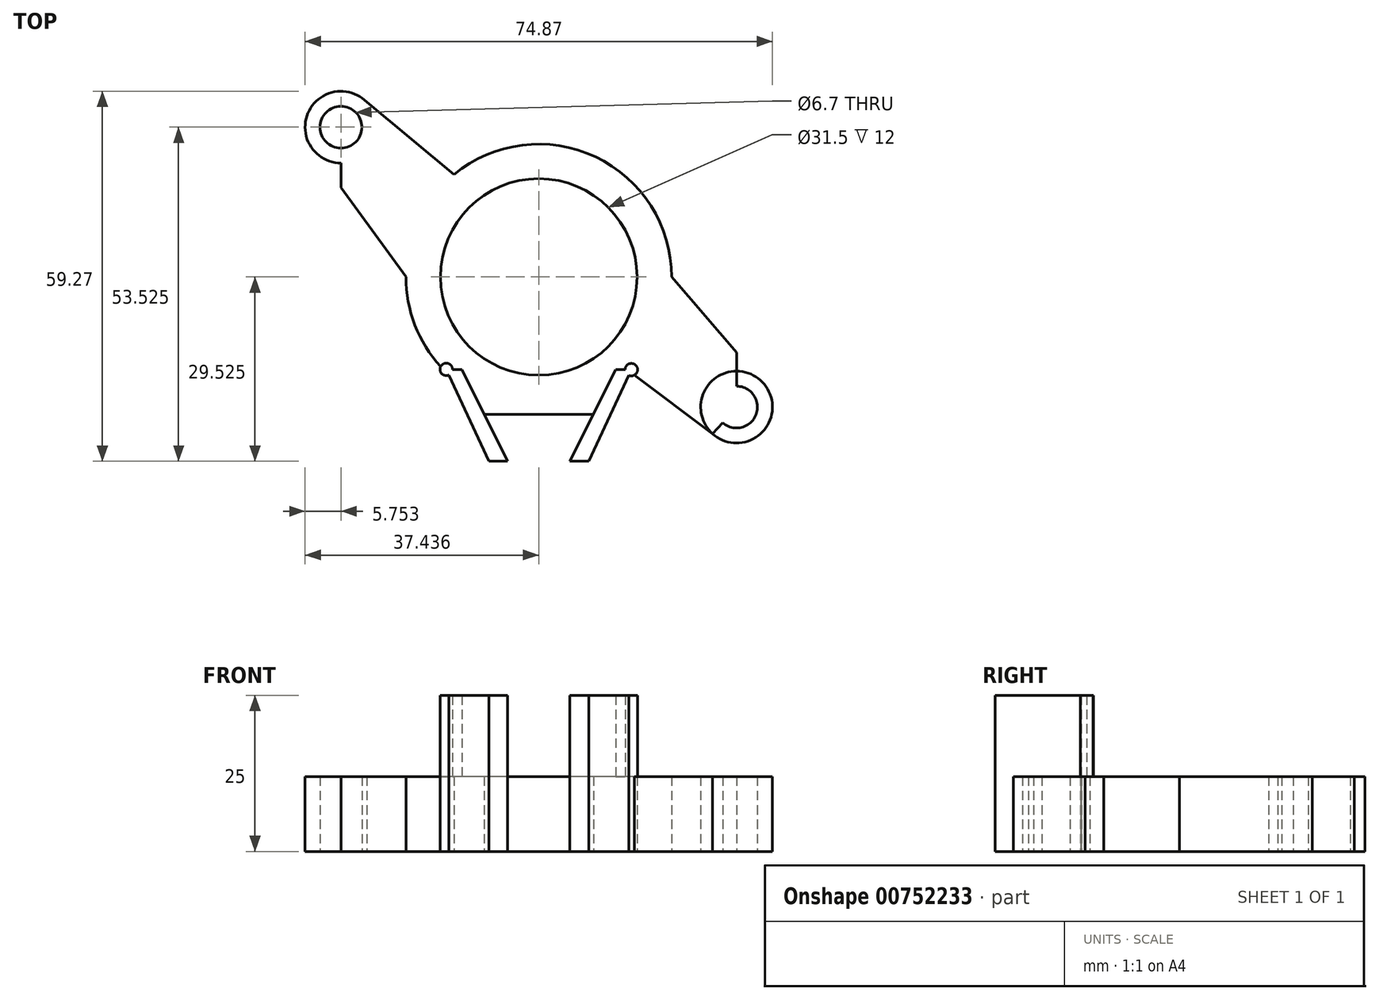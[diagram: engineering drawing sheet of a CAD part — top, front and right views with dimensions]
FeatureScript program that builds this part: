
annotation { "Feature Type Name" : "Feature", "Feature Type Description" : "" }
export const myFeature = defineFeature(function(context is Context, id is Id, definition is map)
    precondition{}
    {
        {
            var Q0;
            Q0=qCreatedBy(makeId("Top.planeOp"),FACE);
            var sketch = newSketch(context, id + "F0", { "sketchPlane" : qUnion([Q0])});
            skLineSegment(sketch, "E0.bottom", {"start": v(-52.47, 39.18) * mm, "end": v(4.2, 39.18) * mm});
            skLineSegment(sketch, "E0.left", {"start": v(-55.82, 35.83) * mm, "end": v(-55.82, -5.47) * mm});
            skLineSegment(sketch, "E0.right", {"start": v(7.55, 35.83) * mm, "end": v(7.55, -2.3) * mm});
            skCircle(sketch, "E1", {"center": v(7.55, 39.18) * mm, "radius": 3.35 * mm});
            skCircle(sketch, "E2", {"center": v(-55.82, 39.18) * mm, "radius": 3.35 * mm});
            skCircle(sketch, "E3", {"center": v(-55.82, -8.82) * mm, "radius": 3.35 * mm});
            skCircle(sketch, "E4", {"center": v(7.55, -5.66) * mm, "radius": 3.35 * mm});
            skCircle(sketch, "E5", {"center": v(-55.82, 39.18) * mm, "radius": 5.75 * mm});
            skCircle(sketch, "E6", {"center": v(7.55, 39.18) * mm, "radius": 5.75 * mm});
            skCircle(sketch, "E7", {"center": v(7.55, -5.66) * mm, "radius": 5.75 * mm});
            skCircle(sketch, "E8", {"center": v(-55.82, -8.82) * mm, "radius": 5.75 * mm});
            skPoint(sketch, "E9.first.point", {"position": v(-24.13, 39.18) * mm});
            skPoint(sketch, "E9.second.point", {"position": v(-55.82, 15.18) * mm});
            skPoint(sketch, "E10.middle", {"position": v(-24.13, 15.18) * mm});
            skCircle(sketch, "E11", {"center": v(-24.13, 15.18) * mm, "radius": 15.75 * mm});
            skLineSegment(sketch, "E12", {"start": v(-24.13, -6.82) * mm, "end": v(-24.13, -7.85) * mm});
            skLineSegment(sketch, "E13", {"start": v(-36.46, 0.34) * mm, "end": v(-29.13, -14.34) * mm});
            skLineSegment(sketch, "E14", {"start": v(-19.13, -14.34) * mm, "end": v(-11.8, 0.34) * mm});
            skLineSegment(sketch, "E15", {"start": v(-29.13, -14.34) * mm, "end": v(-32.13, -14.34) * mm});
            skLineSegment(sketch, "E16", {"start": v(-32.13, -14.34) * mm, "end": v(-38.96, 0.4) * mm});
            skLineSegment(sketch, "E17", {"start": v(-38.96, 0.4) * mm, "end": v(-36.46, 0.34) * mm});
            skLineSegment(sketch, "E18", {"start": v(-19.13, -14.34) * mm, "end": v(-16.13, -14.34) * mm});
            skLineSegment(sketch, "E19", {"start": v(-16.13, -14.34) * mm, "end": v(-9.3, 0.34) * mm});
            skLineSegment(sketch, "E20", {"start": v(-9.3, 0.34) * mm, "end": v(-11.8, 0.34) * mm});
            skLineSegment(sketch, "E21.trimOffspring", {"start": v(-55.82, -8.82) * mm, "end": v(-55.82, -8.82) * mm});
            skLineSegment(sketch, "E22.trimOffspring", {"start": v(7.55, 39.18) * mm, "end": v(7.55, 39.18) * mm});
            skPoint(sketch, "E23.orphan", {"position": v(-24.13, -14.34) * mm});
            skLineSegment(sketch, "E24", {"start": v(-24.13, 15.18) * mm, "end": v(-42.63, 15.18) * mm});
            skLineSegment(sketch, "E25", {"start": v(-36.46, 0.34) * mm, "end": v(-42.63, 15.18) * mm});
            skLineSegment(sketch, "E26", {"start": v(-24.13, 15.18) * mm, "end": v(-5.63, 15.18) * mm});
            skLineSegment(sketch, "E27", {"start": v(-11.8, 0.34) * mm, "end": v(-5.63, 15.18) * mm});
            skLineSegment(sketch, "E28", {"start": v(-29.13, -14.34) * mm, "end": v(-19.13, -14.34) * mm});
            skLineSegment(sketch, "E29", {"start": v(-42.63, 15.18) * mm, "end": v(-55.82, 15.18) * mm});
            skLineSegment(sketch, "E30", {"start": v(-5.63, 15.18) * mm, "end": v(7.55, 15.18) * mm});
            skLineSegment(sketch, "E31", {"start": v(-24.13, 15.18) * mm, "end": v(-24.13, -14.34) * mm});
            skLineSegment(sketch, "E32", {"start": v(-24.13, 15.18) * mm, "end": v(-24.13, 39.18) * mm});
            skLineSegment(sketch, "E33", {"start": v(-24.13, -6.82) * mm, "end": v(1.92, -6.82) * mm});
            skLineSegment(sketch, "E34", {"start": v(-24.13, -6.82) * mm, "end": v(-50.43, -6.82) * mm});
            skLineSegment(sketch, "E35", {"start": v(7.55, -5.66) * mm, "end": v(11.38, -1.37) * mm});
            skLineSegment(sketch, "E36", {"start": v(11.38, -1.37) * mm, "end": v(7.55, -5.66) * mm});
            skLineSegment(sketch, "E37", {"start": v(7.55, -5.66) * mm, "end": v(3.72, -9.95) * mm});
            skLineSegment(sketch, "E38", {"start": v(-55.82, 39.18) * mm, "end": v(-59.94, 35.18) * mm});
            skLineSegment(sketch, "E39", {"start": v(-55.82, 39.18) * mm, "end": v(-51.7, 43.2) * mm});
            skArc(sketch, "E40", {"start": v(-2.85, 15.18) * mm, "mid": v(-32.67, 34.68) * mm, "end": v(-38.57, -0.46) * mm});
            skLineSegment(sketch, "E41", {"start": v(11.38, -1.37) * mm, "end": v(-2.85, 15.18) * mm});
            skLineSegment(sketch, "E42", {"start": v(-51.7, 43.2) * mm, "end": v(-37.7, 31.59) * mm});
            skLineSegment(sketch, "E43", {"start": v(-59.94, 35.18) * mm, "end": v(-45.42, 15.18) * mm});
            skLineSegment(sketch, "E44", {"start": v(3.72, -9.95) * mm, "end": v(-9.47, 0) * mm});
            skLineSegment(sketch, "E45", {"start": v(-36.46, 0.34) * mm, "end": v(-24.13, 0.34) * mm});
            skLineSegment(sketch, "E46", {"start": v(-24.13, 0.34) * mm, "end": v(-11.8, 0.34) * mm});
            skLineSegment(sketch, "E47", {"start": v(-38.96, 0.4) * mm, "end": v(-39.44, 0.4) * mm});
            skCircle(sketch, "E48", {"center": v(-9.3, 0.34) * mm, "radius": 1 * mm});
            skCircle(sketch, "E49", {"center": v(-38.96, 0.4) * mm, "radius": 1 * mm});
            skSolve(sketch);
        }
        {
            var Q0;
            {var subQ0=sQuery(id+"F0.wireOp",EDGE,"E39");var subQ1=sQuery(id+"F0.wireOp",EDGE,"E2");var subQ2=makeQuery(id+"F0.imprint","INTERSECT",VERTEX,{"derivedFrom":[subQ1,subQ0]});Q0=makeQuery(id+"F0.imprint","IMPRINT",FACE,{"disambiguationData":[TD([[makeQuery(id+"F0.imprint","IMPRINT",EDGE,{"disambiguationData":[TD([[subQ2,-1.0]])],"derivedFrom":subQ1}),-1.0]])]});}
            var Q1;
            {var subQ0=sQuery(id+"F0.wireOp",EDGE,"E0.bottom");var subQ1=sQuery(id+"F0.wireOp",EDGE,"E2");var subQ2=makeQuery(id+"F0.imprint","INTERSECT",VERTEX,{"derivedFrom":[subQ1,subQ0]});Q1=makeQuery(id+"F0.imprint","IMPRINT",FACE,{"disambiguationData":[TD([[makeQuery(id+"F0.imprint","IMPRINT",EDGE,{"disambiguationData":[TD([[subQ2,-1.0]])],"derivedFrom":subQ1}),-1.0]])]});}
            var Q2;
            {var subQ0=sQuery(id+"F0.wireOp",EDGE,"E42");var subQ3=sQuery(id+"F0.wireOp",EDGE,"E0.bottom");var subQ5=makeQuery(id+"F0.imprint","INTERSECT",VERTEX,{"derivedFrom":[subQ3,subQ0]});Q2=makeQuery(id+"F0.imprint","IMPRINT",FACE,{"disambiguationData":[TD([[makeQuery(id+"F0.imprint","IMPRINT",EDGE,{"disambiguationData":[TD([[subQ5,1.0]])],"derivedFrom":subQ3}),1.0]])]});}
            var Q3;
            {var subQ0=sQuery(id+"F0.wireOp",EDGE,"E0.left");var subQ1=sQuery(id+"F0.wireOp",EDGE,"E2");var subQ2=makeQuery(id+"F0.imprint","INTERSECT",VERTEX,{"derivedFrom":[subQ1,subQ0]});Q3=makeQuery(id+"F0.imprint","IMPRINT",FACE,{"disambiguationData":[TD([[makeQuery(id+"F0.imprint","IMPRINT",EDGE,{"disambiguationData":[TD([[subQ2,1.0]])],"derivedFrom":subQ1}),-1.0]])]});}
            var Q4;
            {var subQ0=sQuery(id+"F0.wireOp",EDGE,"E0.bottom");var subQ1=sQuery(id+"F0.wireOp",EDGE,"E2");var subQ2=makeQuery(id+"F0.imprint","INTERSECT",VERTEX,{"derivedFrom":[subQ1,subQ0]});Q4=makeQuery(id+"F0.imprint","IMPRINT",FACE,{"disambiguationData":[TD([[makeQuery(id+"F0.imprint","IMPRINT",EDGE,{"disambiguationData":[TD([[subQ2,1.0]])],"derivedFrom":subQ1}),-1.0]])]});}
            var Q5;
            {var subQ0=sQuery(id+"F0.wireOp",EDGE,"E43");var subQ3=sQuery(id+"F0.wireOp",EDGE,"E0.left");var subQ5=makeQuery(id+"F0.imprint","INTERSECT",VERTEX,{"derivedFrom":[subQ3,subQ0]});Q5=makeQuery(id+"F0.imprint","IMPRINT",FACE,{"disambiguationData":[TD([[makeQuery(id+"F0.imprint","IMPRINT",EDGE,{"disambiguationData":[TD([[subQ5,1.0]])],"derivedFrom":subQ3}),-1.0]])]});}
            var Q6;
            {var subQ7=sQuery(id+"F0.wireOp",EDGE,"E5");var subQ9=sQuery(id+"F0.wireOp",EDGE,"E0.bottom");var subQ11=makeQuery(id+"F0.imprint","INTERSECT",VERTEX,{"derivedFrom":[subQ7,subQ9]});Q6=makeQuery(id+"F0.imprint","IMPRINT",FACE,{"disambiguationData":[TD([[makeQuery(id+"F0.imprint","IMPRINT",EDGE,{"disambiguationData":[TD([[subQ11,1.0]])],"derivedFrom":subQ7}),-1.0]])]});}
            var Q7;
            {var subQ0=sQuery(id+"F0.wireOp",EDGE,"E32");var subQ1=sQuery(id+"F0.wireOp",EDGE,"E11");var subQ2=makeQuery(id+"F0.imprint","INTERSECT",VERTEX,{"derivedFrom":[subQ1,subQ0]});Q7=makeQuery(id+"F0.imprint","IMPRINT",FACE,{"disambiguationData":[TD([[makeQuery(id+"F0.imprint","IMPRINT",EDGE,{"disambiguationData":[TD([[subQ2,-1.0]])],"derivedFrom":subQ1}),-1.0]])]});}
            var Q8;
            {var subQ0=sQuery(id+"F0.wireOp",EDGE,"E32");var subQ1=sQuery(id+"F0.wireOp",EDGE,"E11");var subQ2=makeQuery(id+"F0.imprint","INTERSECT",VERTEX,{"derivedFrom":[subQ1,subQ0]});Q8=makeQuery(id+"F0.imprint","IMPRINT",FACE,{"disambiguationData":[TD([[makeQuery(id+"F0.imprint","IMPRINT",EDGE,{"disambiguationData":[TD([[subQ2,1.0]])],"derivedFrom":subQ1}),-1.0]])]});}
            var Q9;
            {var subQ0=sQuery(id+"F0.wireOp",EDGE,"E27");Q9=makeQuery(id+"F0.imprint","IMPRINT",FACE,{"disambiguationData":[TD([[makeQuery(id+"F0.imprint","IMPRINT",EDGE,{"derivedFrom":subQ0}),-1.0]])]});}
            var Q10;
            {var subQ5=sQuery(id+"F0.wireOp",EDGE,"E27");Q10=makeQuery(id+"F0.imprint","IMPRINT",FACE,{"disambiguationData":[TD([[makeQuery(id+"F0.imprint","IMPRINT",EDGE,{"derivedFrom":subQ5}),1.0]])]});}
            var Q11;
            {var subQ0=sQuery(id+"F0.wireOp",EDGE,"E0.right");var subQ1=sQuery(id+"F0.wireOp",EDGE,"E4");var subQ2=makeQuery(id+"F0.imprint","INTERSECT",VERTEX,{"derivedFrom":[subQ1,subQ0]});Q11=makeQuery(id+"F0.imprint","IMPRINT",FACE,{"disambiguationData":[TD([[makeQuery(id+"F0.imprint","IMPRINT",EDGE,{"disambiguationData":[TD([[subQ2,-1.0]])],"derivedFrom":subQ1}),-1.0]])]});}
            var Q12;
            {var subQ0=sQuery(id+"F0.wireOp",EDGE,"E0.right");var subQ1=sQuery(id+"F0.wireOp",EDGE,"E4");var subQ2=makeQuery(id+"F0.imprint","INTERSECT",VERTEX,{"derivedFrom":[subQ1,subQ0]});Q12=makeQuery(id+"F0.imprint","IMPRINT",FACE,{"disambiguationData":[TD([[makeQuery(id+"F0.imprint","IMPRINT",EDGE,{"disambiguationData":[TD([[subQ2,1.0]])],"derivedFrom":subQ1}),-1.0]])]});}
            var Q13;
            {var subQ0=sQuery(id+"F0.wireOp",EDGE,"E36");var subQ1=sQuery(id+"F0.wireOp",EDGE,"E4");var subQ2=makeQuery(id+"F0.imprint","INTERSECT",VERTEX,{"derivedFrom":[subQ1,subQ0]});Q13=makeQuery(id+"F0.imprint","IMPRINT",FACE,{"disambiguationData":[TD([[makeQuery(id+"F0.imprint","IMPRINT",EDGE,{"disambiguationData":[TD([[subQ2,1.0]])],"derivedFrom":subQ1}),-1.0]])]});}
            var Q14;
            {var subQ0=sQuery(id+"F0.wireOp",EDGE,"E33");var subQ1=sQuery(id+"F0.wireOp",EDGE,"E19");var subQ2=makeQuery(id+"F0.imprint","INTERSECT",VERTEX,{"derivedFrom":[subQ1,subQ0]});Q14=makeQuery(id+"F0.imprint","IMPRINT",FACE,{"disambiguationData":[TD([[makeQuery(id+"F0.imprint","IMPRINT",EDGE,{"disambiguationData":[TD([[subQ2,-1.0]])],"derivedFrom":subQ1}),1.0]])]});}
            var Q15;
            {var subQ0=sQuery(id+"F0.wireOp",EDGE,"E18");Q15=makeQuery(id+"F0.imprint","IMPRINT",FACE,{"disambiguationData":[TD([[makeQuery(id+"F0.imprint","IMPRINT",EDGE,{"derivedFrom":subQ0}),1.0]])]});}
            var Q16;
            {var subQ0=sQuery(id+"F0.wireOp",EDGE,"E31");var subQ3=makeQuery(id+"F0.imprint","IMPRINT",VERTEX,{"derivedFrom":subQ0});Q16=makeQuery(id+"F0.imprint","IMPRINT",FACE,{"disambiguationData":[TD([[makeQuery(id+"F0.imprint","IMPRINT",EDGE,{"disambiguationData":[TD([[subQ3,-1.0]])],"derivedFrom":subQ0}),1.0]])]});}
            var Q17;
            {var subQ0=sQuery(id+"F0.wireOp",EDGE,"E15");Q17=makeQuery(id+"F0.imprint","IMPRINT",FACE,{"disambiguationData":[TD([[makeQuery(id+"F0.imprint","IMPRINT",EDGE,{"derivedFrom":subQ0}),-1.0]])]});}
            var Q18;
            {var subQ1=sQuery(id+"F0.wireOp",EDGE,"E31");var subQ3=makeQuery(id+"F0.imprint","IMPRINT",VERTEX,{"derivedFrom":subQ1});Q18=makeQuery(id+"F0.imprint","IMPRINT",FACE,{"disambiguationData":[TD([[makeQuery(id+"F0.imprint","IMPRINT",EDGE,{"disambiguationData":[TD([[subQ3,-1.0]])],"derivedFrom":subQ1}),-1.0]])]});}
            var Q19;
            {var subQ0=sQuery(id+"F0.wireOp",EDGE,"E34");var subQ1=sQuery(id+"F0.wireOp",EDGE,"E16");var subQ2=makeQuery(id+"F0.imprint","INTERSECT",VERTEX,{"derivedFrom":[subQ1,subQ0]});Q19=makeQuery(id+"F0.imprint","IMPRINT",FACE,{"disambiguationData":[TD([[makeQuery(id+"F0.imprint","IMPRINT",EDGE,{"disambiguationData":[TD([[subQ2,-1.0]])],"derivedFrom":subQ1}),-1.0]])]});}
            var Q20;
            {var subQ0=sQuery(id+"F0.wireOp",EDGE,"E45");var subQ7=sQuery(id+"F0.wireOp",EDGE,"E11");var subQ9=makeQuery(id+"F0.imprint","INTERSECT",VERTEX,{"derivedFrom":[subQ7,subQ0]});Q20=makeQuery(id+"F0.imprint","IMPRINT",FACE,{"disambiguationData":[TD([[makeQuery(id+"F0.imprint","IMPRINT",EDGE,{"disambiguationData":[TD([[subQ9,-1.0]])],"derivedFrom":subQ7}),-1.0]])]});}
            var Q21;
            {var subQ1=sQuery(id+"F0.wireOp",EDGE,"E31");var subQ3=sQuery(id+"F0.wireOp",EDGE,"E11");var subQ4=makeQuery(id+"F0.imprint","INTERSECT",VERTEX,{"derivedFrom":[subQ3,subQ1]});Q21=makeQuery(id+"F0.imprint","IMPRINT",FACE,{"disambiguationData":[TD([[makeQuery(id+"F0.imprint","IMPRINT",EDGE,{"disambiguationData":[TD([[subQ4,-1.0]])],"derivedFrom":subQ3}),-1.0]])]});}
            var Q22;
            {var subQ5=sQuery(id+"F0.wireOp",EDGE,"E25");Q22=makeQuery(id+"F0.imprint","IMPRINT",FACE,{"disambiguationData":[TD([[makeQuery(id+"F0.imprint","IMPRINT",EDGE,{"derivedFrom":subQ5}),-1.0]])]});}
            var Q23;
            {var subQ7=sQuery(id+"F0.wireOp",EDGE,"E25");Q23=makeQuery(id+"F0.imprint","IMPRINT",FACE,{"disambiguationData":[TD([[makeQuery(id+"F0.imprint","IMPRINT",EDGE,{"derivedFrom":subQ7}),1.0]])]});}
            var Q24;
            {var subQ0=sQuery(id+"F0.wireOp",EDGE,"E16");var subQ1=makeQuery(id+"F0.imprint","INTERSECT",VERTEX,{"derivedFrom":[subQ0,sQuery(id+"F0.wireOp",EDGE,"E40")]});Q24=makeQuery(id+"F0.imprint","IMPRINT",FACE,{"disambiguationData":[TD([[makeQuery(id+"F0.imprint","IMPRINT",EDGE,{"disambiguationData":[TD([[subQ1,1.0]])],"derivedFrom":subQ0}),-1.0]])]});}
            var Q25;
            {var subQ0=sQuery(id+"F0.wireOp",EDGE,"E47");Q25=makeQuery(id+"F0.imprint","IMPRINT",FACE,{"disambiguationData":[TD([[makeQuery(id+"F0.imprint","IMPRINT",EDGE,{"derivedFrom":subQ0}),-1.0]])]});}
            var Q26;
            {var subQ0=sQuery(id+"F0.wireOp",EDGE,"E40");var subQ1=sQuery(id+"F0.wireOp",EDGE,"E16");var subQ2=makeQuery(id+"F0.imprint","INTERSECT",VERTEX,{"derivedFrom":[subQ1,subQ0]});Q26=makeQuery(id+"F0.imprint","IMPRINT",FACE,{"disambiguationData":[TD([[makeQuery(id+"F0.imprint","IMPRINT",EDGE,{"disambiguationData":[TD([[subQ2,1.0]])],"derivedFrom":subQ1}),1.0]])]});}
            var Q27;
            {var subQ0=sQuery(id+"F0.wireOp",EDGE,"E33");var subQ1=sQuery(id+"F0.wireOp",EDGE,"E7");var subQ2=makeQuery(id+"F0.imprint","INTERSECT",VERTEX,{"derivedFrom":[subQ1,subQ0]});Q27=makeQuery(id+"F0.imprint","IMPRINT",FACE,{"disambiguationData":[TD([[makeQuery(id+"F0.imprint","IMPRINT",EDGE,{"disambiguationData":[TD([[subQ2,1.0]])],"derivedFrom":subQ0}),-1.0]])]});}
            var Q28;
            {var subQ0=sQuery(id+"F0.wireOp",EDGE,"E41");var subQ3=sQuery(id+"F0.wireOp",EDGE,"E0.right");var subQ5=makeQuery(id+"F0.imprint","INTERSECT",VERTEX,{"derivedFrom":[subQ3,subQ0]});Q28=makeQuery(id+"F0.imprint","IMPRINT",FACE,{"disambiguationData":[TD([[makeQuery(id+"F0.imprint","IMPRINT",EDGE,{"disambiguationData":[TD([[subQ5,-1.0]])],"derivedFrom":subQ3}),1.0]])]});}
            var Q29;
            {var subQ0=sQuery(id+"F0.wireOp",EDGE,"E20");var subQ1=sQuery(id+"F0.wireOp",EDGE,"E19");var subQ2=makeQuery(id+"F0.imprint","INTERSECT",VERTEX,{"derivedFrom":[subQ1,subQ0]});Q29=makeQuery(id+"F0.imprint","IMPRINT",FACE,{"disambiguationData":[TD([[makeQuery(id+"F0.imprint","IMPRINT",EDGE,{"disambiguationData":[TD([[subQ2,1.0]])],"derivedFrom":subQ1}),-1.0]])]});}
            var Q30;
            {var subQ0=sQuery(id+"F0.wireOp",EDGE,"E19");var subQ1=makeQuery(id+"F0.imprint","INTERSECT",VERTEX,{"derivedFrom":[subQ0,sQuery(id+"F0.wireOp",EDGE,"E44")]});Q30=makeQuery(id+"F0.imprint","IMPRINT",FACE,{"disambiguationData":[TD([[makeQuery(id+"F0.imprint","IMPRINT",EDGE,{"disambiguationData":[TD([[subQ1,1.0]])],"derivedFrom":subQ0}),1.0]])]});}
            var Q31;
            {var subQ0=sQuery(id+"F0.wireOp",EDGE,"E44");var subQ1=sQuery(id+"F0.wireOp",EDGE,"E19");var subQ2=makeQuery(id+"F0.imprint","INTERSECT",VERTEX,{"derivedFrom":[subQ1,subQ0]});Q31=makeQuery(id+"F0.imprint","IMPRINT",FACE,{"disambiguationData":[TD([[makeQuery(id+"F0.imprint","IMPRINT",EDGE,{"disambiguationData":[TD([[subQ2,1.0]])],"derivedFrom":subQ1}),-1.0]])]});}
            var Q32;
            {var subQ0=sQuery(id+"F0.wireOp",EDGE,"E47");Q32=makeQuery(id+"F0.imprint","IMPRINT",FACE,{"disambiguationData":[TD([[makeQuery(id+"F0.imprint","IMPRINT",EDGE,{"derivedFrom":subQ0}),1.0]])]});}
            extrude(context, id + "F1", {"entities" : qUnion([Q0, Q1, Q2, Q3, Q4, Q5, Q6, Q7, Q8, Q9, Q10, Q11, Q12, Q13, Q14, Q15, Q16, Q17, Q18, Q19, Q20, Q21, Q22, Q23, Q24, Q25, Q26, Q27, Q28, Q29, Q30, Q31, Q32]), "depth" : 12 * mm, "offsetDistance" : 25 * mm});
        }
        {
            var Q0;
            {var subQ0=sQuery(id+"F0.wireOp",EDGE,"E15");Q0=makeQuery(id+"F0.imprint","IMPRINT",FACE,{"disambiguationData":[TD([[makeQuery(id+"F0.imprint","IMPRINT",EDGE,{"derivedFrom":subQ0}),-1.0]])]});}
            var Q1;
            {var subQ0=sQuery(id+"F0.wireOp",EDGE,"E34");var subQ1=sQuery(id+"F0.wireOp",EDGE,"E16");var subQ2=makeQuery(id+"F0.imprint","INTERSECT",VERTEX,{"derivedFrom":[subQ1,subQ0]});Q1=makeQuery(id+"F0.imprint","IMPRINT",FACE,{"disambiguationData":[TD([[makeQuery(id+"F0.imprint","IMPRINT",EDGE,{"disambiguationData":[TD([[subQ2,-1.0]])],"derivedFrom":subQ1}),-1.0]])]});}
            var Q2;
            {var subQ0=sQuery(id+"F0.wireOp",EDGE,"E16");var subQ1=makeQuery(id+"F0.imprint","INTERSECT",VERTEX,{"derivedFrom":[subQ0,sQuery(id+"F0.wireOp",EDGE,"E40")]});Q2=makeQuery(id+"F0.imprint","IMPRINT",FACE,{"disambiguationData":[TD([[makeQuery(id+"F0.imprint","IMPRINT",EDGE,{"disambiguationData":[TD([[subQ1,1.0]])],"derivedFrom":subQ0}),-1.0]])]});}
            var Q3;
            {var subQ0=sQuery(id+"F0.wireOp",EDGE,"E47");Q3=makeQuery(id+"F0.imprint","IMPRINT",FACE,{"disambiguationData":[TD([[makeQuery(id+"F0.imprint","IMPRINT",EDGE,{"derivedFrom":subQ0}),-1.0]])]});}
            var Q4;
            {var subQ0=sQuery(id+"F0.wireOp",EDGE,"E40");var subQ1=sQuery(id+"F0.wireOp",EDGE,"E16");var subQ2=makeQuery(id+"F0.imprint","INTERSECT",VERTEX,{"derivedFrom":[subQ1,subQ0]});Q4=makeQuery(id+"F0.imprint","IMPRINT",FACE,{"disambiguationData":[TD([[makeQuery(id+"F0.imprint","IMPRINT",EDGE,{"disambiguationData":[TD([[subQ2,1.0]])],"derivedFrom":subQ1}),1.0]])]});}
            var Q5;
            {var subQ0=sQuery(id+"F0.wireOp",EDGE,"E47");Q5=makeQuery(id+"F0.imprint","IMPRINT",FACE,{"disambiguationData":[TD([[makeQuery(id+"F0.imprint","IMPRINT",EDGE,{"derivedFrom":subQ0}),1.0]])]});}
            var Q6;
            {var subQ0=sQuery(id+"F0.wireOp",EDGE,"E19");var subQ1=makeQuery(id+"F0.imprint","INTERSECT",VERTEX,{"derivedFrom":[subQ0,sQuery(id+"F0.wireOp",EDGE,"E44")]});Q6=makeQuery(id+"F0.imprint","IMPRINT",FACE,{"disambiguationData":[TD([[makeQuery(id+"F0.imprint","IMPRINT",EDGE,{"disambiguationData":[TD([[subQ1,1.0]])],"derivedFrom":subQ0}),1.0]])]});}
            var Q7;
            {var subQ0=sQuery(id+"F0.wireOp",EDGE,"E20");var subQ1=sQuery(id+"F0.wireOp",EDGE,"E19");var subQ2=makeQuery(id+"F0.imprint","INTERSECT",VERTEX,{"derivedFrom":[subQ1,subQ0]});Q7=makeQuery(id+"F0.imprint","IMPRINT",FACE,{"disambiguationData":[TD([[makeQuery(id+"F0.imprint","IMPRINT",EDGE,{"disambiguationData":[TD([[subQ2,1.0]])],"derivedFrom":subQ1}),-1.0]])]});}
            var Q8;
            {var subQ0=sQuery(id+"F0.wireOp",EDGE,"E44");var subQ1=sQuery(id+"F0.wireOp",EDGE,"E19");var subQ2=makeQuery(id+"F0.imprint","INTERSECT",VERTEX,{"derivedFrom":[subQ1,subQ0]});Q8=makeQuery(id+"F0.imprint","IMPRINT",FACE,{"disambiguationData":[TD([[makeQuery(id+"F0.imprint","IMPRINT",EDGE,{"disambiguationData":[TD([[subQ2,1.0]])],"derivedFrom":subQ1}),-1.0]])]});}
            var Q9;
            {var subQ0=sQuery(id+"F0.wireOp",EDGE,"E33");var subQ1=sQuery(id+"F0.wireOp",EDGE,"E19");var subQ2=makeQuery(id+"F0.imprint","INTERSECT",VERTEX,{"derivedFrom":[subQ1,subQ0]});Q9=makeQuery(id+"F0.imprint","IMPRINT",FACE,{"disambiguationData":[TD([[makeQuery(id+"F0.imprint","IMPRINT",EDGE,{"disambiguationData":[TD([[subQ2,-1.0]])],"derivedFrom":subQ1}),1.0]])]});}
            var Q10;
            {var subQ0=sQuery(id+"F0.wireOp",EDGE,"E18");Q10=makeQuery(id+"F0.imprint","IMPRINT",FACE,{"disambiguationData":[TD([[makeQuery(id+"F0.imprint","IMPRINT",EDGE,{"derivedFrom":subQ0}),1.0]])]});}
            extrude(context, id + "F2", {"entities" : qUnion([Q0, Q1, Q2, Q3, Q4, Q5, Q6, Q7, Q8, Q9, Q10]), "operationType" : NewBodyOperationType.ADD, "depth" : 25 * mm, "offsetDistance" : 25 * mm});
        }
    });
